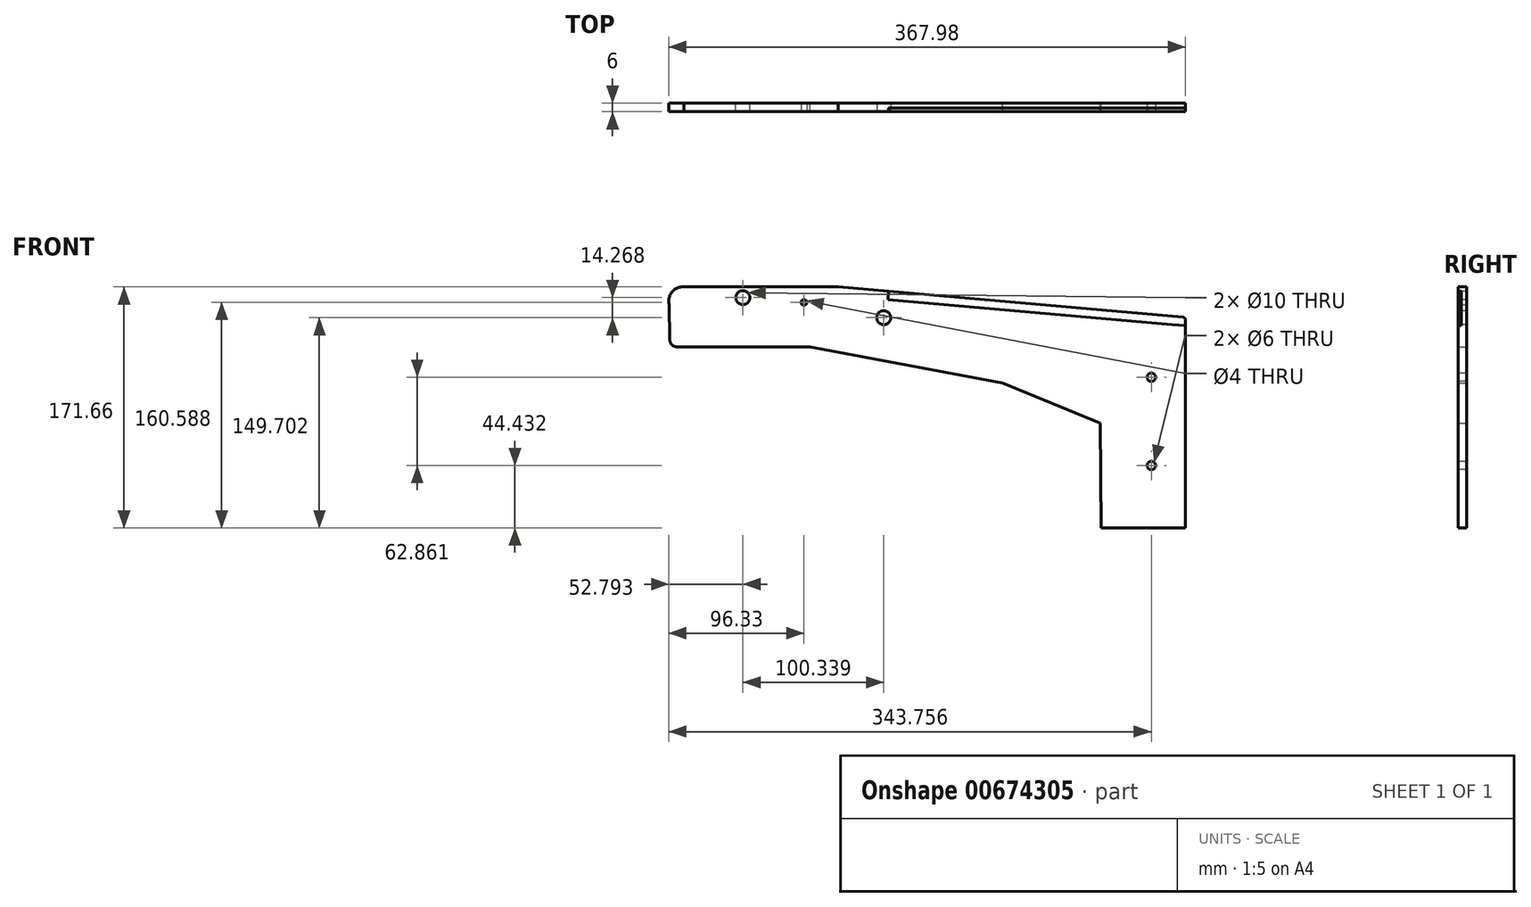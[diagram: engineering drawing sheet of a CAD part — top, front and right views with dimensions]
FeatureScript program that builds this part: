
annotation { "Feature Type Name" : "Feature", "Feature Type Description" : "" }
export const myFeature = defineFeature(function(context is Context, id is Id, definition is map)
    precondition{}
    {
        {
            var Q0;
            Q0=qCreatedBy(makeId("Front.planeOp"),FACE);
            var sketch = newSketch(context, id + "F0", { "sketchPlane" : qUnion([Q0])});
            skLineSegment(sketch, "E0", {"start": v(-49.9, 7.66) * mm, "end": v(60.1, 7.66) * mm});
            skArc(sketch, "E1", {"start": v(-49.9, 7.66) * mm, "mid": v(-58.4, 4) * mm, "end": v(-60.24, -5.07) * mm});
            skLineSegment(sketch, "E2", {"start": v(-49.93, -35) * mm, "end": v(40.07, -35) * mm});
            skLineSegment(sketch, "E3", {"start": v(307.35, -163.97) * mm, "end": v(247.35, -163.97) * mm});
            skLineSegment(sketch, "E4", {"start": v(-60.24, -5.07) * mm, "end": v(-59.88, -30.07) * mm});
            skLineSegment(sketch, "E5", {"start": v(-54.89, -35) * mm, "end": v(-49.93, -35) * mm});
            skPoint(sketch, "E6.visualSharp", {"position": v(-59.81, -35) * mm});
            skArc(sketch, "E6.filletArc", {"start": v(-59.88, -30.07) * mm, "mid": v(-58.4, -33.56) * mm, "end": v(-54.89, -35) * mm});
            skLineSegment(sketch, "E7", {"start": v(177.25, -60.95) * mm, "end": v(246.58, -89.53) * mm});
            skLineSegment(sketch, "E8", {"start": v(60.1, 7.66) * mm, "end": v(307.35, -13.97) * mm});
            skLineSegment(sketch, "E9", {"start": v(40.07, -35) * mm, "end": v(177.25, -60.95) * mm});
            skLineSegment(sketch, "E10", {"start": v(247.35, -163.97) * mm, "end": v(246.58, -89.53) * mm});
            skLineSegment(sketch, "E11", {"start": v(307.35, -163.97) * mm, "end": v(307.35, -13.97) * mm});
            skPoint(sketch, "E12.end.orphan", {"position": v(310.72, 0) * mm});
            skSolve(sketch);
        }
        {
            var Q0;
            Q0 = qSketchRegion(id + "F0", true);
            extrude(context, id + "F1", {"entities" : qUnion([Q0]), "depth" : 6 * mm, "offsetDistance" : 25 * mm});
        }
        {
            var Q0;
            Q0=makeQuery(id+"F1.opExtrude","CAP_FACE",FACE,{"disambiguationData":[OSD([sQuery(id+"F0.wireOp",EDGE,"E0"),sQuery(id+"F0.wireOp",EDGE,"E1"),sQuery(id+"F0.wireOp",EDGE,"E2"),sQuery(id+"F0.wireOp",EDGE,"xIpO2BMK-1Sr3-U6kz-732z-lHFiZcdXaP95"),sQuery(id+"F0.wireOp",EDGE,"E3"),sQuery(id+"F0.wireOp",EDGE,"zyuM4KxI-rK7D-eBj5-RQWG-Z7kNhVQKbpSr"),sQuery(id+"F0.wireOp",EDGE,"E4"),sQuery(id+"F0.wireOp",EDGE,"E5"),sQuery(id+"F0.wireOp",EDGE,"E6.filletArc"),sQuery(id+"F0.wireOp",EDGE,"E7"),sQuery(id+"F0.wireOp",EDGE,"E8"),sQuery(id+"F0.wireOp",EDGE,"E9")])],"isStart":false});
            var sketch = newSketch(context, id + "F2", { "sketchPlane" : qUnion([Q0])});
            skLineSegment(sketch, "E13", {"start": v(-49.88, 0) * mm, "end": v(-60.37, 0) * mm});
            skLineSegment(sketch, "E14", {"start": v(-49.88, 0) * mm, "end": v(30.12, 0) * mm});
            skLineSegment(sketch, "E15", {"start": v(30.12, 0) * mm, "end": v(92.5, -8.77) * mm});
            skLineSegment(sketch, "E16", {"start": v(92.5, -8.77) * mm, "end": v(92.5, -14.27) * mm});
            skCircle(sketch, "E17", {"center": v(92.5, -14.27) * mm, "radius": 5 * mm});
            skSolve(sketch);
        }
        {
            var Q0;
            Q0 = qSketchRegion(id + "F2", true);
            extrude(context, id + "F3", {"entities" : qUnion([Q0]), "operationType" : NewBodyOperationType.REMOVE, "endBound" : BoundingType.THROUGH_ALL, "oppositeDirection" : true, "depth" : 25 * mm, "offsetDistance" : 25 * mm});
        }
        {
            var Q0;
            Q0=makeQuery(id+"F1.opExtrude","CAP_FACE",FACE,{"disambiguationData":[OSD([sQuery(id+"F0.wireOp",EDGE,"E0"),sQuery(id+"F0.wireOp",EDGE,"E1"),sQuery(id+"F0.wireOp",EDGE,"E2"),sQuery(id+"F0.wireOp",EDGE,"xIpO2BMK-1Sr3-U6kz-732z-lHFiZcdXaP95"),sQuery(id+"F0.wireOp",EDGE,"E3"),sQuery(id+"F0.wireOp",EDGE,"zyuM4KxI-rK7D-eBj5-RQWG-Z7kNhVQKbpSr"),sQuery(id+"F0.wireOp",EDGE,"E4"),sQuery(id+"F0.wireOp",EDGE,"E5"),sQuery(id+"F0.wireOp",EDGE,"E6.filletArc"),sQuery(id+"F0.wireOp",EDGE,"E7"),sQuery(id+"F0.wireOp",EDGE,"E8"),sQuery(id+"F0.wireOp",EDGE,"E9")])],"isStart":false});
            var sketch = newSketch(context, id + "F4", { "sketchPlane" : qUnion([Q0])});
            skLineSegment(sketch, "E18", {"start": v(111.62, 3.16) * mm, "end": v(111.62, -8.84) * mm});
            skCircle(sketch, "E19", {"center": v(283.13, -119.54) * mm, "radius": 3 * mm});
            skCircle(sketch, "E20", {"center": v(283.13, -56.68) * mm, "radius": 3 * mm});
            skSolve(sketch);
        }
        {
            var Q0;
            Q0 = qSketchRegion(id + "F4", true);
            extrude(context, id + "F5", {"entities" : qUnion([Q0]), "operationType" : NewBodyOperationType.REMOVE, "endBound" : BoundingType.THROUGH_ALL, "oppositeDirection" : true, "depth" : 25 * mm, "offsetDistance" : 25 * mm});
        }
        {
            var Q0;
            Q0=makeQuery(id+"F1.opExtrude","CAP_FACE",FACE,{"disambiguationData":[OSD([sQuery(id+"F0.wireOp",EDGE,"E0"),sQuery(id+"F0.wireOp",EDGE,"E1"),sQuery(id+"F0.wireOp",EDGE,"E2"),sQuery(id+"F0.wireOp",EDGE,"xIpO2BMK-1Sr3-U6kz-732z-lHFiZcdXaP95"),sQuery(id+"F0.wireOp",EDGE,"E3"),sQuery(id+"F0.wireOp",EDGE,"zyuM4KxI-rK7D-eBj5-RQWG-Z7kNhVQKbpSr"),sQuery(id+"F0.wireOp",EDGE,"E4"),sQuery(id+"F0.wireOp",EDGE,"E5"),sQuery(id+"F0.wireOp",EDGE,"E6.filletArc"),sQuery(id+"F0.wireOp",EDGE,"E7"),sQuery(id+"F0.wireOp",EDGE,"E8"),sQuery(id+"F0.wireOp",EDGE,"E9")])],"isStart":true});
            var sketch = newSketch(context, id + "F6", { "sketchPlane" : qUnion([Q0])});
            skCircle(sketch, "E21", {"center": v(7.84, 0) * mm, "radius": 5 * mm});
            skSolve(sketch);
        }
        {
            var Q0;
            Q0 = qSketchRegion(id + "F6", true);
            extrude(context, id + "F7", {"entities" : qUnion([Q0]), "operationType" : NewBodyOperationType.REMOVE, "endBound" : BoundingType.THROUGH_ALL, "oppositeDirection" : true, "depth" : 25 * mm, "offsetDistance" : 25 * mm});
        }
        {
            var Q0;
            Q0=makeQuery(id+"F1.opExtrude","CAP_FACE",FACE,{"disambiguationData":[OSD([sQuery(id+"F0.wireOp",EDGE,"E0"),sQuery(id+"F0.wireOp",EDGE,"E1"),sQuery(id+"F0.wireOp",EDGE,"E2"),sQuery(id+"F0.wireOp",EDGE,"xIpO2BMK-1Sr3-U6kz-732z-lHFiZcdXaP95"),sQuery(id+"F0.wireOp",EDGE,"E3"),sQuery(id+"F0.wireOp",EDGE,"zyuM4KxI-rK7D-eBj5-RQWG-Z7kNhVQKbpSr"),sQuery(id+"F0.wireOp",EDGE,"E4"),sQuery(id+"F0.wireOp",EDGE,"E5"),sQuery(id+"F0.wireOp",EDGE,"E6.filletArc"),sQuery(id+"F0.wireOp",EDGE,"E7"),sQuery(id+"F0.wireOp",EDGE,"E8"),sQuery(id+"F0.wireOp",EDGE,"E9")])],"isStart":false});
            var sketch = newSketch(context, id + "F8", { "sketchPlane" : qUnion([Q0])});
            skCircle(sketch, "E22", {"center": v(35.7, -3.38) * mm, "radius": 2 * mm});
            skSolve(sketch);
        }
        {
            var Q0;
            Q0 = qSketchRegion(id + "F8", true);
            extrude(context, id + "F9", {"entities" : qUnion([Q0]), "operationType" : NewBodyOperationType.REMOVE, "endBound" : BoundingType.THROUGH_ALL, "oppositeDirection" : true, "depth" : 25 * mm, "offsetDistance" : 25 * mm});
        }
        {
            var Q0;
            Q0=makeQuery(id+"F1.opExtrude","CAP_FACE",FACE,{"disambiguationData":[OSD([sQuery(id+"F0.wireOp",EDGE,"E0"),sQuery(id+"F0.wireOp",EDGE,"E1"),sQuery(id+"F0.wireOp",EDGE,"E2"),sQuery(id+"F0.wireOp",EDGE,"E3"),sQuery(id+"F0.wireOp",EDGE,"E4"),sQuery(id+"F0.wireOp",EDGE,"E5"),sQuery(id+"F0.wireOp",EDGE,"E6.filletArc"),sQuery(id+"F0.wireOp",EDGE,"E7"),sQuery(id+"F0.wireOp",EDGE,"E8"),sQuery(id+"F0.wireOp",EDGE,"E9"),sQuery(id+"F0.wireOp",EDGE,"E10"),sQuery(id+"F0.wireOp",EDGE,"E11")])],"isStart":false});
            var sketch = newSketch(context, id + "F10", { "sketchPlane" : qUnion([Q0])});
            skLineSegment(sketch, "E23", {"start": v(95.99, 4.53) * mm, "end": v(298.21, -13.17) * mm});
            skLineSegment(sketch, "E24", {"start": v(95.46, -1.45) * mm, "end": v(297.69, -19.14) * mm});
            skLineSegment(sketch, "E25", {"start": v(95.99, 4.53) * mm, "end": v(95.46, -1.45) * mm});
            skLineSegment(sketch, "E26", {"start": v(298.21, -13.17) * mm, "end": v(307.35, -13.97) * mm});
            skLineSegment(sketch, "E27", {"start": v(307.35, -13.97) * mm, "end": v(307.35, -19.97) * mm});
            skLineSegment(sketch, "E28", {"start": v(297.69, -19.14) * mm, "end": v(307.35, -19.97) * mm});
            skSolve(sketch);
        }
        {
            var Q0;
            Q0 = qSketchRegion(id + "F10", true);
            extrude(context, id + "F11", {"entities" : qUnion([Q0]), "operationType" : NewBodyOperationType.REMOVE, "oppositeDirection" : true, "depth" : 2.5 * mm, "offsetDistance" : 25 * mm});
        }
        {
            var Q0;
            Q0=makeQuery(id+"F1.opExtrude","SWEPT_EDGE",EDGE,{"disambiguationData":[OSD([sQuery(id+"F0.wireOp",EDGE,"E8"),sQuery(id+"F0.wireOp",EDGE,"E11")])]});
            fillet(context, id + "F12", {"entities" : qUnion([Q0]), "radius" : 2 * mm, "tangentPropagation" : true, "allowEdgeOverflow" : false});
        }
    });
